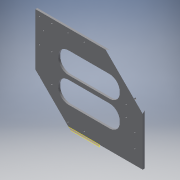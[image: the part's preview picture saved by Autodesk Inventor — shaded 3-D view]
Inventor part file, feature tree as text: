
AUTODESK INVENTOR PART (.ipt)
format: ipt  version: 2016 (Build 200138000, 138)  size: 210,432 bytes
history: native  units: in
note: dims shown in document units (in); Inventor stores cm internally (conversion verified against a paired STEP export)
features: extrude x6, sketch x6, projected_geometry x3, plane x1, fillet x1, reference x1
ambient origin geometry x8: Origin, YZ Plane, XZ Plane, XY Plane, X Axis, Y Axis, Z Axis, Center Point
bodies: Solid1 (feature_tree)
feature tree (18):
  plane  "Work Plane1"
  extrude  "Extrusion1"  Depth=0.24in TaperAngle=0.0deg
  extrude  "Extrusion2"  Depth=2.0in
  extrude  "Extrusion3"  Depth=0.5in
  extrude  "Extrusion4"  Depth=0.175in
  extrude  "Extrusion5"  Depth=1.5in
  extrude  "Extrusion6"  Depth=1.321in TaperAngle=0.0deg
  fillet  "Fillet1"  Radius=0.175in
  sketch  "Sketch1"  dims[d0=13.25in d1=0.24in d2=0.0in]
  sketch  "Sketch2"  dims[d3=2.0in d4=2.0in]
  projected_geometry  "Projected Loop1"
  sketch  "Sketch3"  dims[d5=2.0in d6=0.5in]
  projected_geometry  "Projected Loop2"
  sketch  "Sketch4"  dims[d7=0.175in d8=0.175in]
  projected_geometry  "Projected Loop3"
  sketch  "Sketch5"  dims[d9=0.175in d10=1.5in]
  reference  "Reference1"
  sketch  "Sketch6"  dims[d11=0.175in d12=0.4275in d13=0.0in d20=0.175in d21=0.175in d22=0.175in d23=0.175in d24=0.175in d25=0.175in d26=0.4275in d27=0.0in d31=0.175in d32=0.175in d33=0.175in d37=0.175in d38=0.175in d39=0.4275in d40=0.0in d41=0.4275in d42=0.0in d43=0.5in d44=0.4275in d45=0.0in d46=1.321in]
